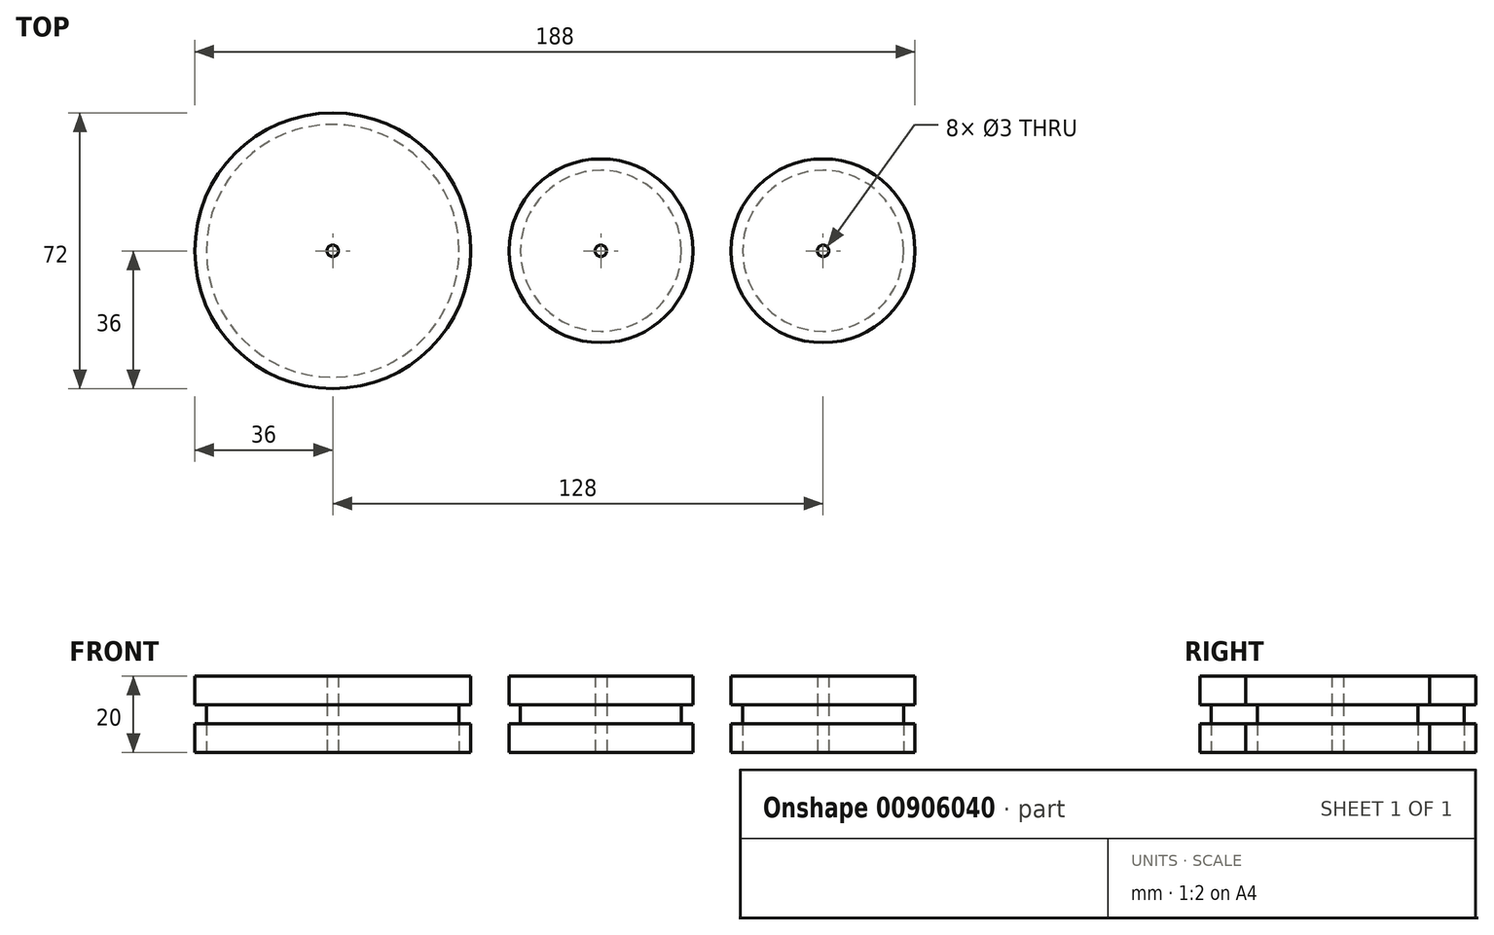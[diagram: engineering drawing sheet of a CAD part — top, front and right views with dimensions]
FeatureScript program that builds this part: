
annotation { "Feature Type Name" : "Feature", "Feature Type Description" : "" }
export const myFeature = defineFeature(function(context is Context, id is Id, definition is map)
    precondition{}
    {
        {
            var Q0;
            Q0=qCreatedBy(makeId("Top.planeOp"),FACE);
            var sketch = newSketch(context, id + "F0", { "sketchPlane" : qUnion([Q0])});
            skCircle(sketch, "E0", {"center": v(0, 0) * mm, "radius": 24 * mm});
            skLineSegment(sketch, "E1", {"start": v(-24, 0) * mm, "end": v(24, 0) * mm});
            skCircle(sketch, "E2", {"center": v(0, 0) * mm, "radius": 21 * mm});
            skLineSegment(sketch, "E3", {"start": v(-21, 0) * mm, "end": v(21, 0) * mm});
            skCircle(sketch, "E4", {"center": v(0, 0) * mm, "radius": 1.5 * mm});
            skLineSegment(sketch, "E5", {"start": v(-1.5, 0) * mm, "end": v(1.5, 0) * mm});
            skSolve(sketch);
        }
        {
            var Q0;
            {var subQ0=sQuery(id+"F0.wireOp",EDGE,"E1");var subQ1=sQuery(id+"F0.wireOp",EDGE,"E0");var subQ2=makeQuery(id+"F0.imprint","INTERSECT",VERTEX,{"disambiguationData":[OD(0.0)],"derivedFrom":[subQ1,subQ0]});Q0=makeQuery(id+"F0.imprint","IMPRINT",FACE,{"disambiguationData":[TD([[makeQuery(id+"F0.imprint","IMPRINT",EDGE,{"disambiguationData":[TD([[subQ2,-1.0]])],"derivedFrom":subQ1}),1.0]])]});}
            var Q1;
            {var subQ0=sQuery(id+"F0.wireOp",EDGE,"E4");var subQ1=sQuery(id+"F0.wireOp",EDGE,"E1");var subQ2=makeQuery(id+"F0.imprint","INTERSECT",VERTEX,{"disambiguationData":[OD(0.0)],"derivedFrom":[subQ1,subQ0]});Q1=makeQuery(id+"F0.imprint","IMPRINT",FACE,{"disambiguationData":[TD([[makeQuery(id+"F0.imprint","IMPRINT",EDGE,{"disambiguationData":[TD([[subQ2,-1.0]])],"derivedFrom":subQ1}),-1.0]])]});}
            var Q2;
            {var subQ0=sQuery(id+"F0.wireOp",EDGE,"E4");var subQ1=sQuery(id+"F0.wireOp",EDGE,"E1");var subQ2=makeQuery(id+"F0.imprint","INTERSECT",VERTEX,{"disambiguationData":[OD(0.0)],"derivedFrom":[subQ1,subQ0]});Q2=makeQuery(id+"F0.imprint","IMPRINT",FACE,{"disambiguationData":[TD([[makeQuery(id+"F0.imprint","IMPRINT",EDGE,{"disambiguationData":[TD([[subQ2,-1.0]])],"derivedFrom":subQ1}),1.0]])]});}
            var Q3;
            {var subQ0=sQuery(id+"F0.wireOp",EDGE,"E1");var subQ1=sQuery(id+"F0.wireOp",EDGE,"E0");var subQ2=makeQuery(id+"F0.imprint","INTERSECT",VERTEX,{"disambiguationData":[OD(0.0)],"derivedFrom":[subQ1,subQ0]});Q3=makeQuery(id+"F0.imprint","IMPRINT",FACE,{"disambiguationData":[TD([[makeQuery(id+"F0.imprint","IMPRINT",EDGE,{"disambiguationData":[TD([[subQ2,1.0]])],"derivedFrom":subQ1}),1.0]])]});}
            extrude(context, id + "F1", {"entities" : qUnion([Q0, Q1, Q2, Q3]), "depth" : 7.5 * mm, "offsetDistance" : 25 * mm});
        }
        {
            var Q0;
            {var subQ0=sQuery(id+"F0.wireOp",EDGE,"E4");var subQ1=sQuery(id+"F0.wireOp",EDGE,"E1");var subQ2=makeQuery(id+"F0.imprint","INTERSECT",VERTEX,{"disambiguationData":[OD(0.0)],"derivedFrom":[subQ1,subQ0]});Q0=makeQuery(id+"F0.imprint","IMPRINT",FACE,{"disambiguationData":[TD([[makeQuery(id+"F0.imprint","IMPRINT",EDGE,{"disambiguationData":[TD([[subQ2,-1.0]])],"derivedFrom":subQ1}),1.0]])]});}
            var Q1;
            {var subQ0=sQuery(id+"F0.wireOp",EDGE,"E4");var subQ1=sQuery(id+"F0.wireOp",EDGE,"E1");var subQ2=makeQuery(id+"F0.imprint","INTERSECT",VERTEX,{"disambiguationData":[OD(0.0)],"derivedFrom":[subQ1,subQ0]});Q1=makeQuery(id+"F0.imprint","IMPRINT",FACE,{"disambiguationData":[TD([[makeQuery(id+"F0.imprint","IMPRINT",EDGE,{"disambiguationData":[TD([[subQ2,-1.0]])],"derivedFrom":subQ1}),-1.0]])]});}
            extrude(context, id + "F2", {"entities" : qUnion([Q0, Q1]), "operationType" : NewBodyOperationType.ADD, "depth" : 12.5 * mm, "offsetDistance" : 25 * mm});
        }
        {
            var Q0;
            {var subQ0=sQuery(id+"F0.wireOp",EDGE,"E4");var subQ1=sQuery(id+"F0.wireOp",EDGE,"E1");var subQ2=makeQuery(id+"F0.imprint","INTERSECT",VERTEX,{"disambiguationData":[OD(0.0)],"derivedFrom":[subQ1,subQ0]});Q0=makeQuery(id+"F0.imprint","IMPRINT",FACE,{"disambiguationData":[TD([[makeQuery(id+"F0.imprint","IMPRINT",EDGE,{"disambiguationData":[TD([[subQ2,-1.0]])],"derivedFrom":subQ1}),1.0]])]});}
            var Q1;
            {var subQ0=sQuery(id+"F0.wireOp",EDGE,"E4");var subQ1=sQuery(id+"F0.wireOp",EDGE,"E1");var subQ2=makeQuery(id+"F0.imprint","INTERSECT",VERTEX,{"disambiguationData":[OD(0.0)],"derivedFrom":[subQ1,subQ0]});Q1=makeQuery(id+"F0.imprint","IMPRINT",FACE,{"disambiguationData":[TD([[makeQuery(id+"F0.imprint","IMPRINT",EDGE,{"disambiguationData":[TD([[subQ2,-1.0]])],"derivedFrom":subQ1}),-1.0]])]});}
            var Q2;
            {var subQ0=sQuery(id+"F0.wireOp",EDGE,"E1");var subQ1=sQuery(id+"F0.wireOp",EDGE,"E0");var subQ2=makeQuery(id+"F0.imprint","INTERSECT",VERTEX,{"disambiguationData":[OD(0.0)],"derivedFrom":[subQ1,subQ0]});Q2=makeQuery(id+"F0.imprint","IMPRINT",FACE,{"disambiguationData":[TD([[makeQuery(id+"F0.imprint","IMPRINT",EDGE,{"disambiguationData":[TD([[subQ2,1.0]])],"derivedFrom":subQ1}),1.0]])]});}
            var Q3;
            {var subQ0=sQuery(id+"F0.wireOp",EDGE,"E1");var subQ1=sQuery(id+"F0.wireOp",EDGE,"E0");var subQ2=makeQuery(id+"F0.imprint","INTERSECT",VERTEX,{"disambiguationData":[OD(0.0)],"derivedFrom":[subQ1,subQ0]});Q3=makeQuery(id+"F0.imprint","IMPRINT",FACE,{"disambiguationData":[TD([[makeQuery(id+"F0.imprint","IMPRINT",EDGE,{"disambiguationData":[TD([[subQ2,-1.0]])],"derivedFrom":subQ1}),1.0]])]});}
            extrude(context, id + "F3", {"entities" : qUnion([Q0, Q1, Q2, Q3]), "depth" : 20 * mm, "offsetDistance" : 25 * mm, "hasSecondDirection" : true, "secondDirectionOppositeDirection" : true, "secondDirectionDepth" : -12.5 * mm});
        }
        {
            var Q0;
            Q0=qCreatedBy(makeId("Top.planeOp"),FACE);
            var sketch = newSketch(context, id + "F4", { "sketchPlane" : qUnion([Q0])});
            skCircle(sketch, "E6", {"center": v(-70, 0) * mm, "radius": 36 * mm});
            skCircle(sketch, "E7", {"center": v(-70, 0) * mm, "radius": 33 * mm});
            skLineSegment(sketch, "E8", {"start": v(-106, 0) * mm, "end": v(-103, 0) * mm});
            skLineSegment(sketch, "E9", {"start": v(-103, 0) * mm, "end": v(-70, 0) * mm});
            skLineSegment(sketch, "E10", {"start": v(-70, 0) * mm, "end": v(-37, 0) * mm});
            skLineSegment(sketch, "E11", {"start": v(-34, 0) * mm, "end": v(-37, 0) * mm});
            skCircle(sketch, "E12", {"center": v(-70, 0) * mm, "radius": 1.5 * mm});
            skCircle(sketch, "E13", {"center": v(58, 0) * mm, "radius": 1.5 * mm});
            skCircle(sketch, "E14", {"center": v(58, 0) * mm, "radius": 21 * mm});
            skCircle(sketch, "E15", {"center": v(58, 0) * mm, "radius": 24 * mm});
            skSolve(sketch);
        }
        {
            var Q0;
            {var subQ0=sQuery(id+"F4.wireOp",EDGE,"E9");var subQ5=sQuery(id+"F4.wireOp",EDGE,"E12");var subQ6=makeQuery(id+"F4.imprint","INTERSECT",VERTEX,{"derivedFrom":[subQ0,subQ5]});Q0=makeQuery(id+"F4.imprint","IMPRINT",FACE,{"disambiguationData":[TD([[makeQuery(id+"F4.imprint","IMPRINT",EDGE,{"disambiguationData":[TD([[subQ6,1.0]])],"derivedFrom":subQ5}),-1.0]])]});}
            var Q1;
            {var subQ0=sQuery(id+"F4.wireOp",EDGE,"E9");var subQ5=sQuery(id+"F4.wireOp",EDGE,"E12");var subQ7=makeQuery(id+"F4.imprint","INTERSECT",VERTEX,{"derivedFrom":[subQ0,subQ5]});Q1=makeQuery(id+"F4.imprint","IMPRINT",FACE,{"disambiguationData":[TD([[makeQuery(id+"F4.imprint","IMPRINT",EDGE,{"disambiguationData":[TD([[subQ7,-1.0]])],"derivedFrom":subQ5}),-1.0]])]});}
            var Q2;
            {var subQ0=sQuery(id+"F4.wireOp",EDGE,"E8");Q2=makeQuery(id+"F4.imprint","IMPRINT",FACE,{"disambiguationData":[TD([[makeQuery(id+"F4.imprint","IMPRINT",EDGE,{"derivedFrom":subQ0}),-1.0]])]});}
            var Q3;
            {var subQ0=sQuery(id+"F4.wireOp",EDGE,"E8");Q3=makeQuery(id+"F4.imprint","IMPRINT",FACE,{"disambiguationData":[TD([[makeQuery(id+"F4.imprint","IMPRINT",EDGE,{"derivedFrom":subQ0}),1.0]])]});}
            var Q4;
            Q4=makeQuery(id+"F4.imprint","IMPRINT",FACE,{"disambiguationData":[TD([[makeQuery(id+"F4.imprint","IMPRINT",EDGE,{"derivedFrom":sQuery(id+"F4.wireOp",EDGE,"E14")}),-1.0]])]});
            var Q5;
            Q5=makeQuery(id+"F4.imprint","IMPRINT",FACE,{"disambiguationData":[TD([[makeQuery(id+"F4.imprint","IMPRINT",EDGE,{"derivedFrom":sQuery(id+"F4.wireOp",EDGE,"E13")}),-1.0]])]});
            extrude(context, id + "F5", {"entities" : qUnion([Q0, Q1, Q2, Q3, Q4, Q5]), "depth" : 7.5 * mm, "offsetDistance" : 25 * mm});
        }
        {
            var Q0;
            {var subQ0=sQuery(id+"F4.wireOp",EDGE,"E9");var subQ5=sQuery(id+"F4.wireOp",EDGE,"E12");var subQ6=makeQuery(id+"F4.imprint","INTERSECT",VERTEX,{"derivedFrom":[subQ0,subQ5]});Q0=makeQuery(id+"F4.imprint","IMPRINT",FACE,{"disambiguationData":[TD([[makeQuery(id+"F4.imprint","IMPRINT",EDGE,{"disambiguationData":[TD([[subQ6,1.0]])],"derivedFrom":subQ5}),-1.0]])]});}
            var Q1;
            {var subQ0=sQuery(id+"F4.wireOp",EDGE,"E9");var subQ5=sQuery(id+"F4.wireOp",EDGE,"E12");var subQ7=makeQuery(id+"F4.imprint","INTERSECT",VERTEX,{"derivedFrom":[subQ0,subQ5]});Q1=makeQuery(id+"F4.imprint","IMPRINT",FACE,{"disambiguationData":[TD([[makeQuery(id+"F4.imprint","IMPRINT",EDGE,{"disambiguationData":[TD([[subQ7,-1.0]])],"derivedFrom":subQ5}),-1.0]])]});}
            var Q2;
            Q2=makeQuery(id+"F4.imprint","IMPRINT",FACE,{"disambiguationData":[TD([[makeQuery(id+"F4.imprint","IMPRINT",EDGE,{"derivedFrom":sQuery(id+"F4.wireOp",EDGE,"E13")}),-1.0]])]});
            extrude(context, id + "F6", {"entities" : qUnion([Q0, Q1, Q2]), "depth" : 12.5 * mm, "offsetDistance" : 25 * mm});
        }
        {
            var Q0;
            {var subQ0=sQuery(id+"F4.wireOp",EDGE,"E9");var subQ5=sQuery(id+"F4.wireOp",EDGE,"E12");var subQ7=makeQuery(id+"F4.imprint","INTERSECT",VERTEX,{"derivedFrom":[subQ0,subQ5]});Q0=makeQuery(id+"F4.imprint","IMPRINT",FACE,{"disambiguationData":[TD([[makeQuery(id+"F4.imprint","IMPRINT",EDGE,{"disambiguationData":[TD([[subQ7,-1.0]])],"derivedFrom":subQ5}),-1.0]])]});}
            var Q1;
            {var subQ0=sQuery(id+"F4.wireOp",EDGE,"E9");var subQ5=sQuery(id+"F4.wireOp",EDGE,"E12");var subQ6=makeQuery(id+"F4.imprint","INTERSECT",VERTEX,{"derivedFrom":[subQ0,subQ5]});Q1=makeQuery(id+"F4.imprint","IMPRINT",FACE,{"disambiguationData":[TD([[makeQuery(id+"F4.imprint","IMPRINT",EDGE,{"disambiguationData":[TD([[subQ6,1.0]])],"derivedFrom":subQ5}),-1.0]])]});}
            var Q2;
            {var subQ0=sQuery(id+"F4.wireOp",EDGE,"E8");Q2=makeQuery(id+"F4.imprint","IMPRINT",FACE,{"disambiguationData":[TD([[makeQuery(id+"F4.imprint","IMPRINT",EDGE,{"derivedFrom":subQ0}),1.0]])]});}
            var Q3;
            {var subQ0=sQuery(id+"F4.wireOp",EDGE,"E8");Q3=makeQuery(id+"F4.imprint","IMPRINT",FACE,{"disambiguationData":[TD([[makeQuery(id+"F4.imprint","IMPRINT",EDGE,{"derivedFrom":subQ0}),-1.0]])]});}
            var Q4;
            Q4=makeQuery(id+"F4.imprint","IMPRINT",FACE,{"disambiguationData":[TD([[makeQuery(id+"F4.imprint","IMPRINT",EDGE,{"derivedFrom":sQuery(id+"F4.wireOp",EDGE,"E13")}),-1.0]])]});
            var Q5;
            Q5=makeQuery(id+"F4.imprint","IMPRINT",FACE,{"disambiguationData":[TD([[makeQuery(id+"F4.imprint","IMPRINT",EDGE,{"derivedFrom":sQuery(id+"F4.wireOp",EDGE,"E14")}),-1.0]])]});
            extrude(context, id + "F7", {"entities" : qUnion([Q0, Q1, Q2, Q3, Q4, Q5]), "depth" : 20 * mm, "offsetDistance" : 25 * mm, "hasSecondDirection" : true, "secondDirectionOppositeDirection" : true, "secondDirectionDepth" : -12.5 * mm});
        }
    });
